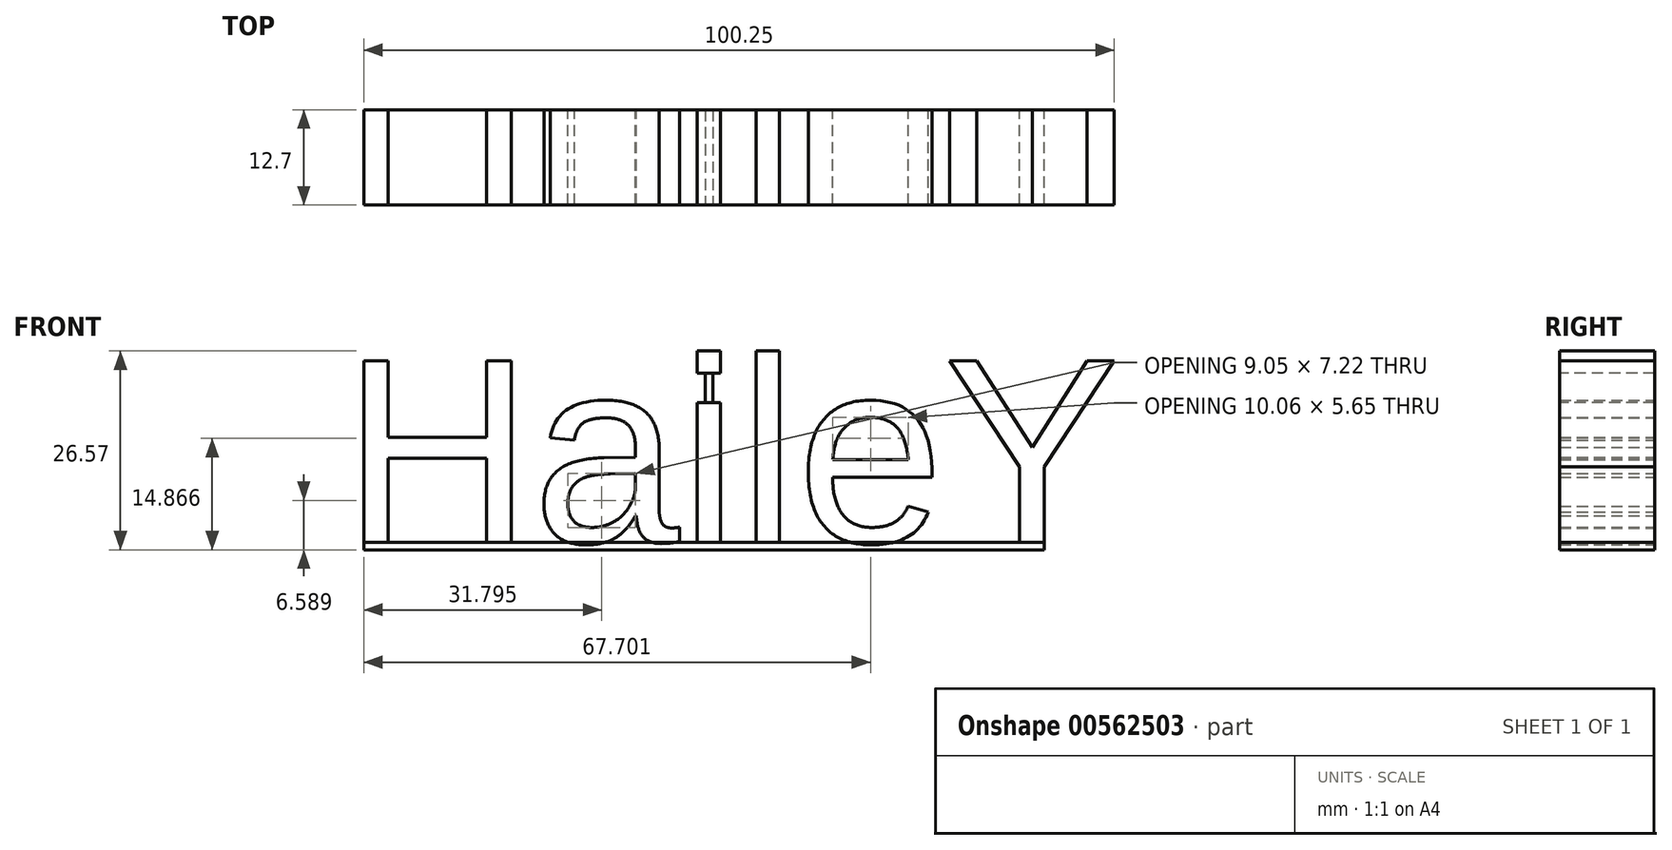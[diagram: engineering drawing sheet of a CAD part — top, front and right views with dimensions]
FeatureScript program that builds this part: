
annotation { "Feature Type Name" : "Feature", "Feature Type Description" : "" }
export const myFeature = defineFeature(function(context is Context, id is Id, definition is map)
    precondition{}
    {
        {
            var Q0;
            Q0=qCreatedBy(makeId("Front.planeOp"),FACE);
            var sketch = newSketch(context, id + "F0", { "sketchPlane" : qUnion([Q0])});
            skText(sketch, "E0", { "text": "HaileY", "fontName": "Arimo-Regular.ttf"});
            skPoint(sketch, "E1", {"position": v(0, 12.7) * mm});
            const initialGuessF0  = {"E0": [-0.0528, 0, 1, 0, 0.0254]};
            skSetInitialGuess(sketch, initialGuessF0);
            skSolve(sketch);
        }
        {
            var Q0;
            Q0=qSketchRegion(id+"F0",true);
            extrude(context, id + "F1", {"entities" : qUnion([Q0]), "endBound" : BoundingType.SYMMETRIC, "depth" : 12.7 * mm, "offsetDistance" : 25.4 * mm});
        }
        {
            var Q0;
            Q0=qCreatedBy(makeId("Top.planeOp"),FACE);
            var sketch = newSketch(context, id + "F2", { "sketchPlane" : qUnion([Q0])});
            skLineSegment(sketch, "E2.0", {"start": v(-49.9, -6.35) * mm, "end": v(-49.9, 6.35) * mm});
            skLineSegment(sketch, "E3.0", {"start": v(40.98, -6.35) * mm, "end": v(40.98, 6.35) * mm});
            skLineSegment(sketch, "E4", {"start": v(-49.9, -6.35) * mm, "end": v(40.98, -6.35) * mm});
            skLineSegment(sketch, "E5", {"start": v(40.98, 6.35) * mm, "end": v(-49.9, 6.35) * mm});
            skSolve(sketch);
        }
        {
            var Q0;
            Q0=makeQuery(id+"F2.imprint","IMPRINT",FACE,{"disambiguationData":[TD([[makeQuery(id+"F2.imprint","IMPRINT",EDGE,{"derivedFrom":sQuery(id+"F2.wireOp",EDGE,"E2.0")}),-1.0]])]});
            extrude(context, id + "F3", {"entities" : qUnion([Q0]), "oppositeDirection" : true, "depth" : 1 * mm, "offsetDistance" : 25.4 * mm});
        }
        {
            var Q0;
            Q0=makeQuery(id+"F1.opExtrude","CAP_FACE",FACE,{"disambiguationData":[OSD([sQuery(id+"F0.wireOp",EDGE,"E0.sketch_text.stroke-51"),sQuery(id+"F0.wireOp",EDGE,"E0.sketch_text.stroke-52"),sQuery(id+"F0.wireOp",EDGE,"E0.sketch_text.stroke-53"),sQuery(id+"F0.wireOp",EDGE,"E0.sketch_text.stroke-54")])],"isStart":false});
            var sketch = newSketch(context, id + "F4", { "sketchPlane" : qUnion([Q0])});
            skPoint(sketch, "E6.0", {"position": v(-3.79, 22.6) * mm});
            skPoint(sketch, "E7.0", {"position": v(-3.79, 18.64) * mm});
            skLineSegment(sketch, "E8", {"start": v(-3.79, 22.6) * mm, "end": v(-3.79, 18.64) * mm, "construction": true});
            skLineSegment(sketch, "E9.bottom", {"start": v(-4.29, 22.6) * mm, "end": v(-3.29, 22.6) * mm});
            skLineSegment(sketch, "E9.top", {"start": v(-4.29, 18.64) * mm, "end": v(-3.29, 18.64) * mm});
            skLineSegment(sketch, "E9.left", {"start": v(-4.29, 22.6) * mm, "end": v(-4.29, 18.64) * mm});
            skLineSegment(sketch, "E9.right", {"start": v(-3.29, 22.6) * mm, "end": v(-3.29, 18.64) * mm});
            skSolve(sketch);
        }
        {
            var Q0;
            Q0=makeQuery(id+"F4.imprint","IMPRINT",FACE,{"disambiguationData":[TD([[makeQuery(id+"F4.imprint","IMPRINT",EDGE,{"derivedFrom":sQuery(id+"F4.wireOp",EDGE,"E9.bottom")}),-1.0]])]});
            var Q1;
            Q1=makeQuery(id+"F1.opExtrude","CAP_FACE",FACE,{"disambiguationData":[OSD([sQuery(id+"F0.wireOp",EDGE,"E0.sketch_text.stroke-47"),sQuery(id+"F0.wireOp",EDGE,"E0.sketch_text.stroke-48"),sQuery(id+"F0.wireOp",EDGE,"E0.sketch_text.stroke-49"),sQuery(id+"F0.wireOp",EDGE,"E0.sketch_text.stroke-50")])],"isStart":true});
            extrude(context, id + "F5", {"entities" : qUnion([Q0]), "endBound" : BoundingType.UP_TO_SURFACE, "oppositeDirection" : true, "depth" : 25.4 * mm, "endBoundEntityFace" : qUnion([Q1]), "offsetDistance" : 25.4 * mm});
        }
    });
